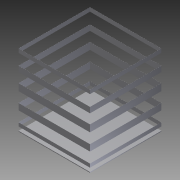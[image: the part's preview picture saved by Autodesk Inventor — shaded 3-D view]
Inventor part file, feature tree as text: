
AUTODESK INVENTOR PART (.ipt)
format: ipt  version: 2011 SP2 (Build 150309200, 309)  size: 134,144 bytes
history: native  units: mm
features: extrude x3, sketch x3
ambient origin geometry x8: Origin, YZ Plane, XZ Plane, XY Plane, X Axis, Y Axis, Z Axis, Center Point
bodies: Solid1 (feature_tree)
feature tree (6):
  extrude  "Extrusion1"  Depth=200.0mm
  extrude  "Extrusion2"  Depth=0.2mm
  extrude  "Extrusion3"  Depth=0.2mm
  sketch  "Sketch1"  dims[d0=200.0mm d1=200.0mm]
  sketch  "Sketch2"  dims[d2=2.0mm d3=0.0mm d4=0.2mm]
  sketch  "Sketch3"  dims[d5=0.2mm d6=0.2mm d7=0.2mm d8=200.0mm d9=2.0mm d10=0.0mm d11=0.0mm d12=200.0mm d13=0.0mm]
